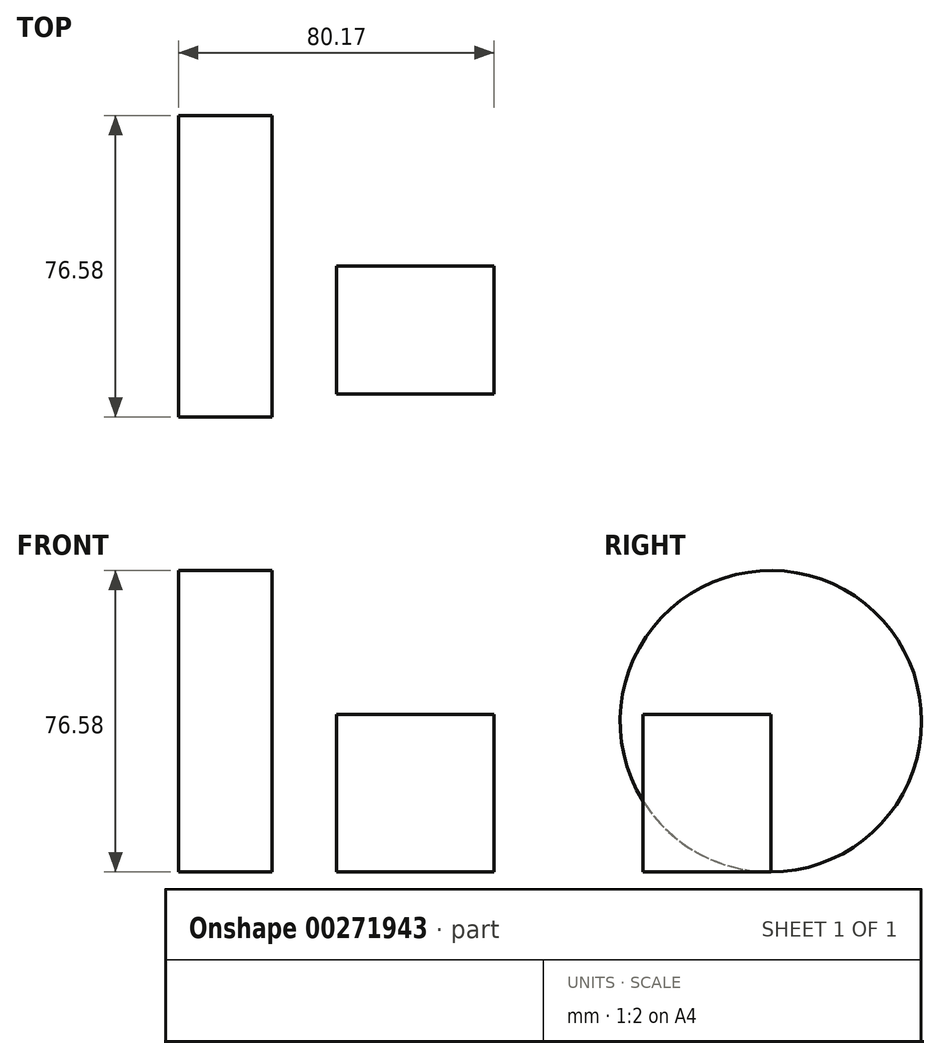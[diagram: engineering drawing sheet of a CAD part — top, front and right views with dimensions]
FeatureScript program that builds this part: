
annotation { "Feature Type Name" : "Feature", "Feature Type Description" : "" }
export const myFeature = defineFeature(function(context is Context, id is Id, definition is map)
    precondition{}
    {
        {
            var Q0;
            Q0=qCreatedBy(makeId("Front.planeOp"),FACE);
            var sketch = newSketch(context, id + "F0", { "sketchPlane" : qUnion([Q0])});
            skLineSegment(sketch, "E0.bottom", {"start": v(0, 40) * mm, "end": v(40, 40) * mm});
            skLineSegment(sketch, "E0.top", {"start": v(0, 0) * mm, "end": v(40, 0) * mm});
            skLineSegment(sketch, "E0.left", {"start": v(0, 40) * mm, "end": v(0, 0) * mm});
            skLineSegment(sketch, "E0.right", {"start": v(40, 40) * mm, "end": v(40, 0) * mm});
            skSolve(sketch);
        }
        {
            var Q0;
            Q0 = qSketchRegion(id + "F0", true);
            extrude(context, id + "F1", {"entities" : qUnion([Q0]), "depth" : 32.5 * mm});
        }
        {
            var Q0;
            Q0=qCreatedBy(makeId("Front.planeOp"),FACE);
            var sketch = newSketch(context, id + "F2", { "sketchPlane" : qUnion([Q0])});
            skLineSegment(sketch, "E1.bottom", {"start": v(-40.17, 38.3) * mm, "end": v(-16.47, 38.3) * mm});
            skLineSegment(sketch, "E1.top", {"start": v(-40.17, 0) * mm, "end": v(-16.47, 0) * mm});
            skLineSegment(sketch, "E1.left", {"start": v(-40.17, 38.3) * mm, "end": v(-40.17, 0) * mm});
            skLineSegment(sketch, "E1.right", {"start": v(-16.47, 38.3) * mm, "end": v(-16.47, 0) * mm});
            skLineSegment(sketch, "E2", {"start": v(-40.17, 38.3) * mm, "end": v(-65.6, 38.3) * mm, "construction": true});
            skSolve(sketch);
        }
        {
            var Q0;
            Q0 = qSketchRegion(id + "F2", true);
            var Q1;
            Q1=sQuery(id+"F2.wireOp",EDGE,"E2");
            revolve(context, id + "F3", {"entities" : qUnion([Q0]), "axis" : qUnion([Q1]), "revolveType" : RevolveType.FULL});
        }
    });
